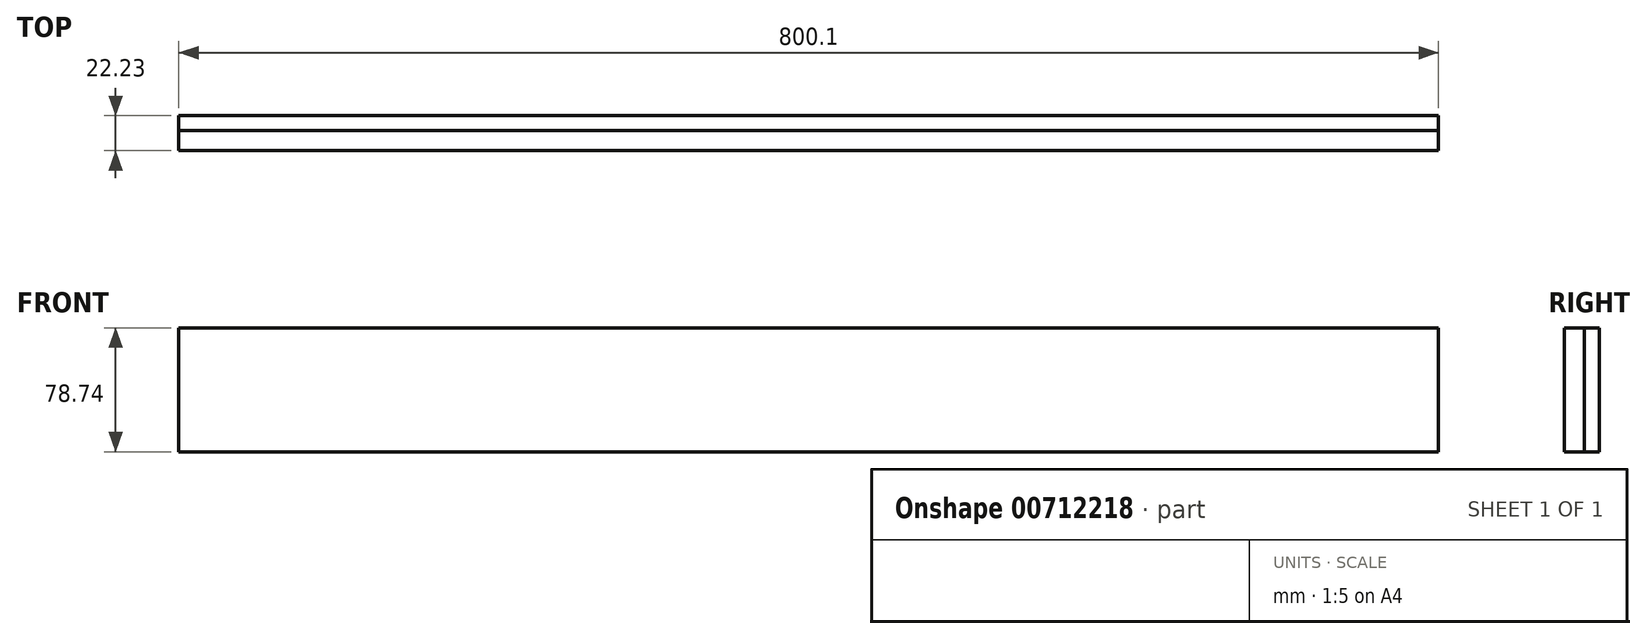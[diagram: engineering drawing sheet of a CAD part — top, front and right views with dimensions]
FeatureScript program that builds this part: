
annotation { "Feature Type Name" : "Feature", "Feature Type Description" : "" }
export const myFeature = defineFeature(function(context is Context, id is Id, definition is map)
    precondition{}
    {
        {
            var Q0;
            Q0=qCreatedBy(makeId("Front.planeOp"),FACE);
            var sketch = newSketch(context, id + "F0", { "sketchPlane" : qUnion([Q0])});
            skLineSegment(sketch, "E0.bottom", {"start": v(-373.28, 0) * mm, "end": v(426.82, 0) * mm});
            skLineSegment(sketch, "E0.top", {"start": v(-373.28, 78.74) * mm, "end": v(426.82, 78.74) * mm});
            skLineSegment(sketch, "E0.left", {"start": v(-373.28, 0) * mm, "end": v(-373.28, 78.74) * mm});
            skLineSegment(sketch, "E0.right", {"start": v(426.82, 0) * mm, "end": v(426.82, 78.74) * mm});
            skSolve(sketch);
        }
        {
            var Q0;
            Q0=makeQuery(id+"F0.imprint","IMPRINT",FACE,{"disambiguationData":[TD([[makeQuery(id+"F0.imprint","IMPRINT",EDGE,{"derivedFrom":sQuery(id+"F0.wireOp",EDGE,"E0.bottom")}),1.0]])]});
            extrude(context, id + "F1", {"entities" : qUnion([Q0]), "depth" : 12.7 * mm, "offsetDistance" : 25.4 * mm});
        }
        {
            var Q0;
            Q0=makeQuery(id+"F1.opExtrude","CAP_FACE",FACE,{"disambiguationData":[OSD([sQuery(id+"F0.wireOp",EDGE,"E0.bottom"),sQuery(id+"F0.wireOp",EDGE,"E0.top"),sQuery(id+"F0.wireOp",EDGE,"E0.left"),sQuery(id+"F0.wireOp",EDGE,"E0.right")])],"isStart":true});
            var sketch = newSketch(context, id + "F2", { "sketchPlane" : qUnion([Q0])});
            skLineSegment(sketch, "E1.bottom", {"start": v(-426.82, 78.74) * mm, "end": v(373.28, 78.74) * mm});
            skLineSegment(sketch, "E1.top", {"start": v(-426.82, 0) * mm, "end": v(373.28, 0) * mm});
            skLineSegment(sketch, "E1.left", {"start": v(-426.82, 78.74) * mm, "end": v(-426.82, 0) * mm});
            skLineSegment(sketch, "E1.right", {"start": v(373.28, 78.74) * mm, "end": v(373.28, 0) * mm});
            skSolve(sketch);
        }
        {
            var Q0;
            Q0=makeQuery(id+"F2.imprint","IMPRINT",FACE,{"disambiguationData":[TD([[makeQuery(id+"F2.imprint","IMPRINT",EDGE,{"derivedFrom":sQuery(id+"F2.wireOp",EDGE,"E1.bottom")}),1.0]])]});
            extrude(context, id + "F3", {"entities" : qUnion([Q0]), "depth" : 9.52 * mm, "offsetDistance" : 25.4 * mm});
        }
    });
